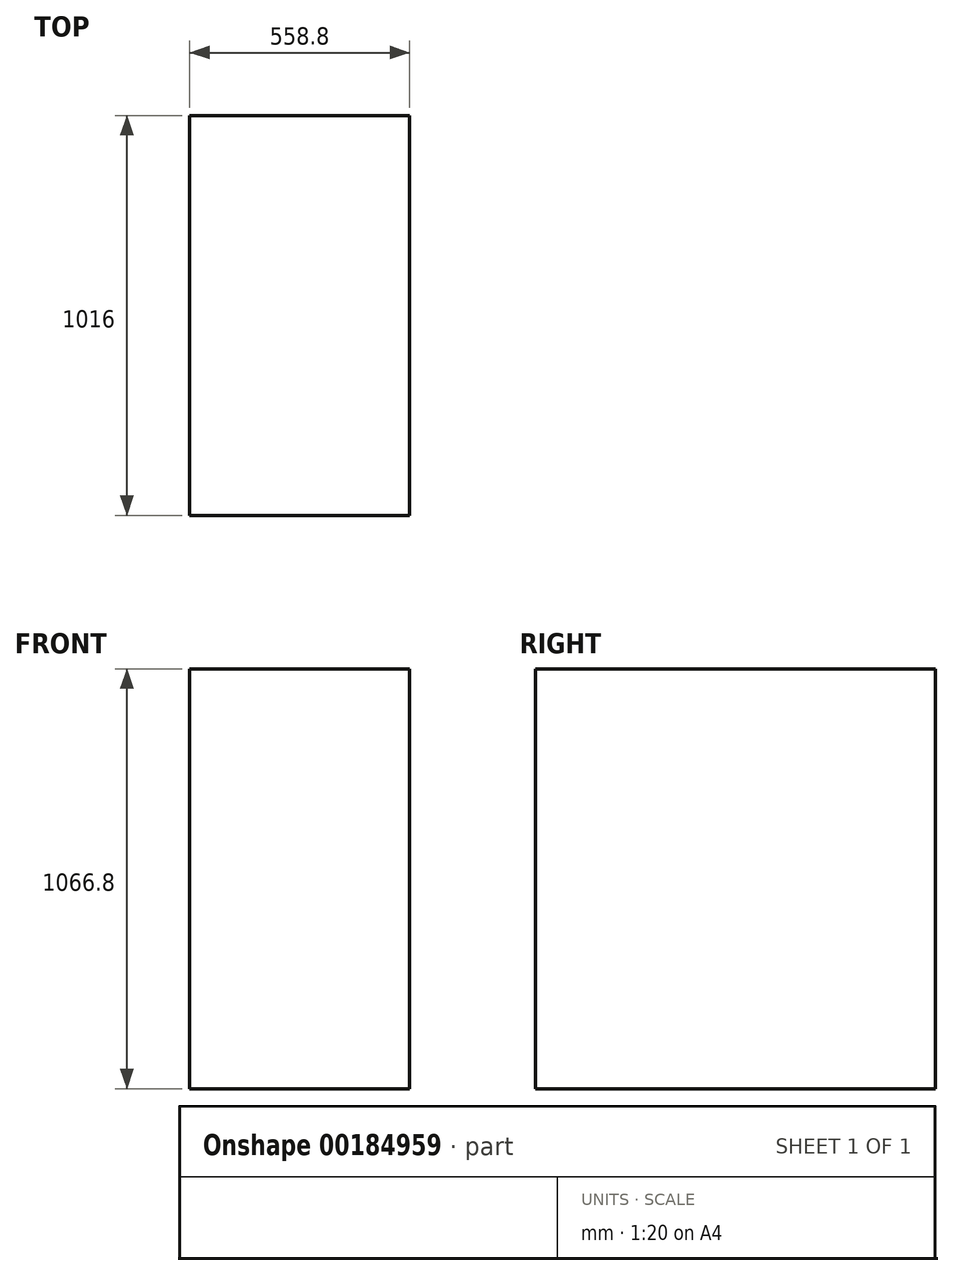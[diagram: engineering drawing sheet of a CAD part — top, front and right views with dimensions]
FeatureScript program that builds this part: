
annotation { "Feature Type Name" : "Feature", "Feature Type Description" : "" }
export const myFeature = defineFeature(function(context is Context, id is Id, definition is map)
    precondition{}
    {
        {
            var Q0;
            Q0=qCreatedBy(makeId("Top.planeOp"),FACE);
            var sketch = newSketch(context, id + "F0", { "sketchPlane" : qUnion([Q0])});
            skLineSegment(sketch, "E0.bottom", {"start": v(279.4, 508) * mm, "end": v(-279.4, 508) * mm});
            skLineSegment(sketch, "E0.top", {"start": v(279.4, -508) * mm, "end": v(-279.4, -508) * mm});
            skLineSegment(sketch, "E0.left", {"start": v(279.4, 508) * mm, "end": v(279.4, -508) * mm});
            skLineSegment(sketch, "E0.right", {"start": v(-279.4, 508) * mm, "end": v(-279.4, -508) * mm});
            skPoint(sketch, "E0.middle", {"position": v(0, 0) * mm});
            skSolve(sketch);
        }
        {
            var Q0;
            Q0=makeQuery(id+"F0.imprint","IMPRINT",FACE,{"disambiguationData":[TD([[makeQuery(id+"F0.imprint","IMPRINT",EDGE,{"derivedFrom":sQuery(id+"F0.wireOp",EDGE,"E0.bottom")}),1.0]])]});
            extrude(context, id + "F1", {"entities" : qUnion([Q0]), "depth" : 1066.8 * mm});
        }
    });
